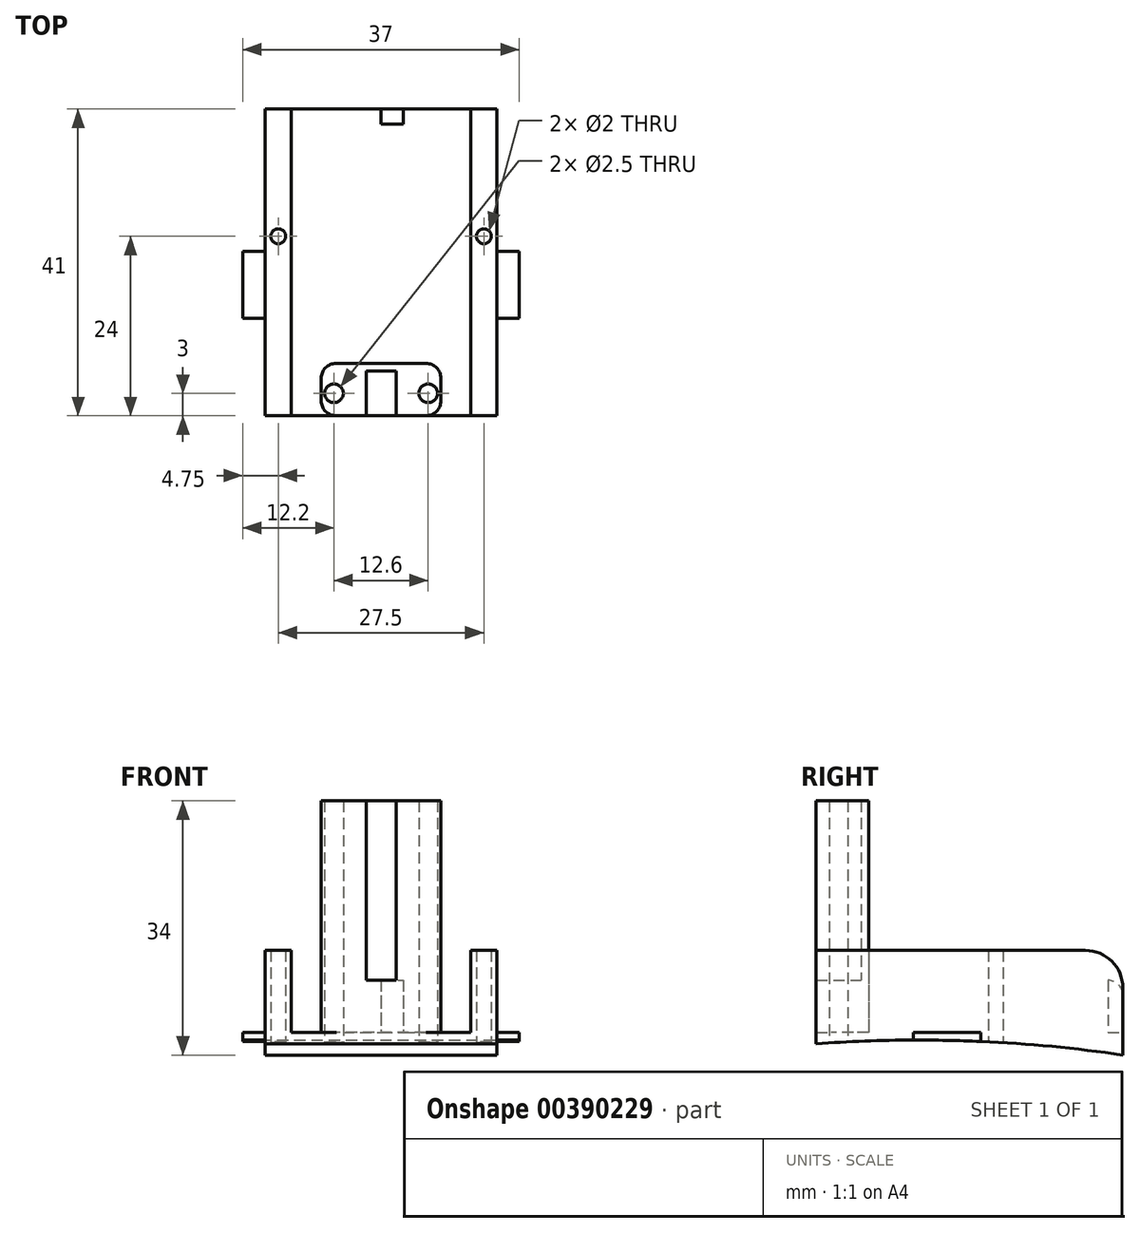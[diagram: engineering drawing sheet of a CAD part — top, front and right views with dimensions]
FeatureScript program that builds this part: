
annotation { "Feature Type Name" : "Feature", "Feature Type Description" : "" }
export const myFeature = defineFeature(function(context is Context, id is Id, definition is map)
    precondition{}
    {
        {
            var Q0;
            Q0=qCreatedBy(makeId("Top.planeOp"),FACE);
            var sketch = newSketch(context, id + "F0", { "sketchPlane" : qUnion([Q0])});
            skLineSegment(sketch, "E0", {"start": v(-15.5, 41) * mm, "end": v(15.5, 41) * mm});
            skLineSegment(sketch, "E1", {"start": v(15.5, 41) * mm, "end": v(15.5, 0) * mm});
            skLineSegment(sketch, "E2", {"start": v(15.5, 0) * mm, "end": v(-15.5, 0) * mm});
            skLineSegment(sketch, "E3", {"start": v(-15.5, 0) * mm, "end": v(-15.5, 41) * mm});
            skLineSegment(sketch, "E4", {"start": v(-12, 41) * mm, "end": v(-12, 0) * mm});
            skLineSegment(sketch, "E5", {"start": v(12, 41) * mm, "end": v(12, 0) * mm});
            skPoint(sketch, "E6.endSnap0", {"position": v(0, 41) * mm});
            skLineSegment(sketch, "E7", {"start": v(0, 39) * mm, "end": v(0, 41) * mm});
            skLineSegment(sketch, "E8", {"start": v(12, 7) * mm, "end": v(-12, 7) * mm});
            skLineSegment(sketch, "E9", {"start": v(-2, 0) * mm, "end": v(-2, 6) * mm});
            skLineSegment(sketch, "E10", {"start": v(-2, 6) * mm, "end": v(2, 6) * mm});
            skLineSegment(sketch, "E11", {"start": v(2, 6) * mm, "end": v(2, 0) * mm});
            skPoint(sketch, "E12", {"position": v(6.3, 3) * mm});
            skPoint(sketch, "E12.positionSnap0", {"position": v(2, 3) * mm});
            skPoint(sketch, "E13", {"position": v(-6.3, 3) * mm});
            skPoint(sketch, "E13.positionSnap0", {"position": v(-2, 3) * mm});
            skLineSegment(sketch, "E14", {"start": v(-15.5, 22) * mm, "end": v(-18.5, 22) * mm});
            skLineSegment(sketch, "E15", {"start": v(-18.5, 22) * mm, "end": v(-18.5, 13) * mm});
            skLineSegment(sketch, "E16", {"start": v(-18.5, 13) * mm, "end": v(-15.5, 13) * mm});
            skLineSegment(sketch, "E17", {"start": v(15.5, 22) * mm, "end": v(18.5, 22) * mm});
            skLineSegment(sketch, "E18", {"start": v(18.5, 22) * mm, "end": v(18.5, 13) * mm});
            skLineSegment(sketch, "E19", {"start": v(18.5, 13) * mm, "end": v(15.5, 13) * mm});
            skLineSegment(sketch, "E20", {"start": v(0, 39) * mm, "end": v(3, 39) * mm});
            skLineSegment(sketch, "E21", {"start": v(3, 39) * mm, "end": v(3, 41) * mm});
            skLineSegment(sketch, "E22", {"start": v(8, 7) * mm, "end": v(8, 0) * mm});
            skLineSegment(sketch, "E23", {"start": v(-8, 7) * mm, "end": v(-8, 0) * mm});
            skPoint(sketch, "E24", {"position": v(-13.75, 24) * mm});
            skPoint(sketch, "E25", {"position": v(13.75, 24) * mm});
            skSolve(sketch);
        }
        {
            var Q0;
            {var subQ3=sQuery(id+"F0.wireOp",EDGE,"E23");Q0=makeQuery(id+"F0.imprint","IMPRINT",FACE,{"disambiguationData":[TD([[makeQuery(id+"F0.imprint","IMPRINT",EDGE,{"derivedFrom":subQ3}),-1.0]])]});}
            var Q1;
            {var subQ10=sQuery(id+"F0.wireOp",EDGE,"E7");Q1=makeQuery(id+"F0.imprint","IMPRINT",FACE,{"disambiguationData":[TD([[makeQuery(id+"F0.imprint","IMPRINT",EDGE,{"derivedFrom":subQ10}),1.0]])]});}
            var Q2;
            {var subQ3=sQuery(id+"F0.wireOp",EDGE,"E22");Q2=makeQuery(id+"F0.imprint","IMPRINT",FACE,{"disambiguationData":[TD([[makeQuery(id+"F0.imprint","IMPRINT",EDGE,{"derivedFrom":subQ3}),1.0]])]});}
            extrude(context, id + "F1", {"entities" : qUnion([Q0, Q1, Q2]), "depth" : 3 * mm});
        }
        {
            var Q0;
            {var subQ0=sQuery(id+"F0.wireOp",EDGE,"E3");var subQ7=sQuery(id+"F0.wireOp",EDGE,"E0");var subQ8=makeQuery(id+"F0.imprint","INTERSECT",VERTEX,{"derivedFrom":[subQ7,subQ0]});Q0=makeQuery(id+"F0.imprint","IMPRINT",FACE,{"disambiguationData":[TD([[makeQuery(id+"F0.imprint","IMPRINT",EDGE,{"disambiguationData":[TD([[subQ8,-1.0]])],"derivedFrom":subQ7}),-1.0]])]});}
            var Q1;
            {var subQ1=sQuery(id+"F0.wireOp",EDGE,"E1");var subQ5=sQuery(id+"F0.wireOp",EDGE,"E0");var subQ6=makeQuery(id+"F0.imprint","INTERSECT",VERTEX,{"derivedFrom":[subQ5,subQ1]});Q1=makeQuery(id+"F0.imprint","IMPRINT",FACE,{"disambiguationData":[TD([[makeQuery(id+"F0.imprint","IMPRINT",EDGE,{"disambiguationData":[TD([[subQ6,1.0]])],"derivedFrom":subQ5}),-1.0]])]});}
            extrude(context, id + "F2", {"entities" : qUnion([Q0, Q1]), "operationType" : NewBodyOperationType.ADD, "depth" : 14 * mm});
        }
        {
            var Q0;
            {var subQ0=sQuery(id+"F0.wireOp",EDGE,"E14");Q0=makeQuery(id+"F0.imprint","IMPRINT",FACE,{"disambiguationData":[TD([[makeQuery(id+"F0.imprint","IMPRINT",EDGE,{"derivedFrom":subQ0}),1.0]])]});}
            var Q1;
            {var subQ0=sQuery(id+"F0.wireOp",EDGE,"E17");Q1=makeQuery(id+"F0.imprint","IMPRINT",FACE,{"disambiguationData":[TD([[makeQuery(id+"F0.imprint","IMPRINT",EDGE,{"derivedFrom":subQ0}),-1.0]])]});}
            extrude(context, id + "F3", {"entities" : qUnion([Q0, Q1]), "operationType" : NewBodyOperationType.ADD, "depth" : 3 * mm});
        }
        {
            var Q0;
            {var subQ0=sQuery(id+"F0.wireOp",EDGE,"E9");Q0=makeQuery(id+"F0.imprint","IMPRINT",FACE,{"disambiguationData":[TD([[makeQuery(id+"F0.imprint","IMPRINT",EDGE,{"derivedFrom":subQ0}),1.0]])]});}
            extrude(context, id + "F4", {"entities" : qUnion([Q0]), "operationType" : NewBodyOperationType.ADD, "depth" : 34 * mm});
        }
        {
            var Q0;
            {var subQ0=sQuery(id+"F0.wireOp",EDGE,"E9");Q0=makeQuery(id+"F0.imprint","IMPRINT",FACE,{"disambiguationData":[TD([[makeQuery(id+"F0.imprint","IMPRINT",EDGE,{"derivedFrom":subQ0}),-1.0]])]});}
            extrude(context, id + "F5", {"entities" : qUnion([Q0]), "operationType" : NewBodyOperationType.ADD, "depth" : 10 * mm});
        }
        {
            var Q0;
            Q0=makeQuery(id+"F5.opExtrude","CAP_EDGE",EDGE,{"disambiguationData":[OSD([sQuery(id+"F0.wireOp",EDGE,"E10")])],"isStart":false});
            var Q1;
            {var subQ0=sQuery(id+"F0.wireOp",EDGE,"E0");Q1=makeQuery(id+"F2.opExtrude","CAP_EDGE",EDGE,{"disambiguationData":[OSD([subQ0]),TDD([makeQuery(id+"F0.imprint","IMPRINT",EDGE,{"disambiguationData":[TD([[makeQuery(id+"F0.imprint","INTERSECT",VERTEX,{"derivedFrom":[subQ0,sQuery(id+"F0.wireOp",EDGE,"E3")]}),-1.0]])],"derivedFrom":subQ0})])],"isStart":false});}
            var Q2;
            {var subQ0=sQuery(id+"F0.wireOp",EDGE,"E0");Q2=makeQuery(id+"F2.opExtrude","CAP_EDGE",EDGE,{"disambiguationData":[OSD([subQ0]),TDD([makeQuery(id+"F0.imprint","IMPRINT",EDGE,{"disambiguationData":[TD([[makeQuery(id+"F0.imprint","INTERSECT",VERTEX,{"derivedFrom":[subQ0,sQuery(id+"F0.wireOp",EDGE,"E1")]}),1.0]])],"derivedFrom":subQ0})])],"isStart":false});}
            fillet(context, id + "F6", {"entities" : qUnion([Q0, Q1, Q2]), "radius" : 5 * mm, "tangentPropagation" : true, "allowEdgeOverflow" : false});
        }
        {
            var Q0;
            {var subQ0=sQuery(id+"F0.wireOp",EDGE,"E7");Q0=makeQuery(id+"F0.imprint","IMPRINT",FACE,{"disambiguationData":[TD([[makeQuery(id+"F0.imprint","IMPRINT",EDGE,{"derivedFrom":subQ0}),-1.0]])]});}
            extrude(context, id + "F7", {"entities" : qUnion([Q0]), "operationType" : NewBodyOperationType.ADD, "depth" : 10 * mm});
        }
        {
            var Q0;
            Q0=makeQuery(id+"F1.opExtrude","CAP_EDGE",EDGE,{"disambiguationData":[OSD([sQuery(id+"F0.wireOp",EDGE,"E23")])],"isStart":false});
            var Q1;
            Q1=makeQuery(id+"F1.opExtrude","CAP_EDGE",EDGE,{"disambiguationData":[OSD([sQuery(id+"F0.wireOp",EDGE,"E22")])],"isStart":false});
            var Q2;
            Q2=makeQuery(id+"F1.opExtrude","CAP_EDGE",EDGE,{"disambiguationData":[OSD([sQuery(id+"F0.wireOp",EDGE,"E4")])],"isStart":false});
            var Q3;
            Q3=makeQuery(id+"F1.opExtrude","CAP_EDGE",EDGE,{"disambiguationData":[OSD([sQuery(id+"F0.wireOp",EDGE,"E5")])],"isStart":false});
            var Q4;
            Q4=makeQuery(id+"F1.opExtrude","CAP_EDGE",EDGE,{"disambiguationData":[OSD([sQuery(id+"F0.wireOp",EDGE,"E8")])],"isStart":false});
            var Q5;
            Q5=makeQuery(id+"F1.opExtrude","CAP_EDGE",EDGE,{"disambiguationData":[OSD([sQuery(id+"F0.wireOp",EDGE,"E20")])],"isStart":false});
            var Q6;
            Q6=makeQuery(id+"F7.opExtrude","CAP_EDGE",EDGE,{"disambiguationData":[OSD([sQuery(id+"F0.wireOp",EDGE,"E0")])],"isStart":false});
            var Q7;
            Q7=makeQuery(id+"F4.opExtrude","SWEPT_EDGE",EDGE,{"disambiguationData":[OSD([sQuery(id+"F0.wireOp",EDGE,"E8"),sQuery(id+"F0.wireOp",EDGE,"E22")])]});
            var Q8;
            Q8=makeQuery(id+"F4.opExtrude","SWEPT_EDGE",EDGE,{"disambiguationData":[OSD([sQuery(id+"F0.wireOp",EDGE,"E8"),sQuery(id+"F0.wireOp",EDGE,"E23")])]});
            var Q9;
            Q9=makeQuery(id+"F4.opExtrude","SWEPT_EDGE",EDGE,{"disambiguationData":[OSD([sQuery(id+"F0.wireOp",EDGE,"E2"),sQuery(id+"F0.wireOp",EDGE,"E22")])]});
            var Q10;
            Q10=makeQuery(id+"F4.opExtrude","SWEPT_EDGE",EDGE,{"disambiguationData":[OSD([sQuery(id+"F0.wireOp",EDGE,"E2"),sQuery(id+"F0.wireOp",EDGE,"E23")])]});
            fillet(context, id + "F8", {"entities" : qUnion([Q0, Q1, Q2, Q3, Q4, Q5, Q6, Q7, Q8, Q9, Q10]), "radius" : 2 * mm, "tangentPropagation" : true, "allowEdgeOverflow" : false});
        }
        {
            var Q0;
            Q0=qCreatedBy(makeId("Right.planeOp"),FACE);
            cPlane(context, id + "F9", {"entities" : qUnion([Q0]), "cplaneType" : CPlaneType.OFFSET, "offset" : 18.9 * mm, "width" : 150 * mm, "height" : 150 * mm});
        }
        {
            var Q0;
            Q0=qCreatedBy(id+"F9.planeOp",FACE);
            var sketch = newSketch(context, id + "F10", { "sketchPlane" : qUnion([Q0])});
            skLineSegment(sketch, "E26", {"start": v(41, 0) * mm, "end": v(0, 0) * mm});
            skLineSegment(sketch, "E27", {"start": v(0, 0) * mm, "end": v(0, 1.5) * mm});
            skArc(sketch, "E28", {"start": v(41, 0) * mm, "mid": v(20.54, 1.87) * mm, "end": v(0, 1.5) * mm});
            skSolve(sketch);
        }
        {
            var Q0;
            Q0=makeQuery(id+"F10.imprint","IMPRINT",FACE,{"disambiguationData":[TD([[makeQuery(id+"F10.imprint","IMPRINT",EDGE,{"derivedFrom":sQuery(id+"F10.wireOp",EDGE,"q8iaQYBd-D0QU-K8Ez-FoIt-P6ilia72zXyT")}),1.0]])]});
            var Q1;
            Q1=makeQuery(id+"F10.imprint","IMPRINT",FACE,{"disambiguationData":[TD([[makeQuery(id+"F10.imprint","IMPRINT",EDGE,{"derivedFrom":sQuery(id+"F10.wireOp",EDGE,"E26")}),-1.0]])]});
            extrude(context, id + "F11", {"entities" : qUnion([Q0, Q1]), "operationType" : NewBodyOperationType.REMOVE, "endBound" : BoundingType.THROUGH_ALL, "oppositeDirection" : true, "depth" : 25 * mm});
        }
        {
            var Q0;
            Q0=sQuery(id+"F0.wireOp",VERTEX,"E24");
            var Q1;
            Q1=sQuery(id+"F0.wireOp",VERTEX,"E25");
            var Q2;
            Q2=makeQuery(id+"F1.opExtrude","SWEPT_BODY",BODY,{"disambiguationData":[OSD([sQuery(id+"F0.wireOp",EDGE,"E0"),sQuery(id+"F0.wireOp",EDGE,"E2"),sQuery(id+"F0.wireOp",EDGE,"E4"),sQuery(id+"F0.wireOp",EDGE,"E5"),sQuery(id+"F0.wireOp",EDGE,"E7"),sQuery(id+"F0.wireOp",EDGE,"E8"),sQuery(id+"F0.wireOp",EDGE,"E20"),sQuery(id+"F0.wireOp",EDGE,"E21"),sQuery(id+"F0.wireOp",EDGE,"E22"),sQuery(id+"F0.wireOp",EDGE,"E23")])]});
            hole(context, id + "F12", {"style" : HoleStyle.SIMPLE, "endStyle" : HoleEndStyle.THROUGH, "oppositeDirection" : true, "holeDiameter" : 2 * mm, "isTappedThrough" : true, "tappedDepth" : 12 * mm, "tapClearance" : 3, "locations" : qUnion([Q0, Q1]), "scope" : qUnion([Q2])});
        }
        {
            var Q0;
            Q0=sQuery(id+"F0.wireOp",VERTEX,"E13");
            var Q1;
            Q1=sQuery(id+"F0.wireOp",VERTEX,"E12");
            var Q2;
            Q2=makeQuery(id+"F1.opExtrude","SWEPT_BODY",BODY,{"disambiguationData":[OSD([sQuery(id+"F0.wireOp",EDGE,"E0"),sQuery(id+"F0.wireOp",EDGE,"E2"),sQuery(id+"F0.wireOp",EDGE,"E4"),sQuery(id+"F0.wireOp",EDGE,"E5"),sQuery(id+"F0.wireOp",EDGE,"E7"),sQuery(id+"F0.wireOp",EDGE,"E8"),sQuery(id+"F0.wireOp",EDGE,"E20"),sQuery(id+"F0.wireOp",EDGE,"E21"),sQuery(id+"F0.wireOp",EDGE,"E22"),sQuery(id+"F0.wireOp",EDGE,"E23")])]});
            hole(context, id + "F13", {"style" : HoleStyle.SIMPLE, "endStyle" : HoleEndStyle.THROUGH, "oppositeDirection" : true, "holeDiameter" : 2.5 * mm, "isTappedThrough" : true, "tappedDepth" : 12 * mm, "tapClearance" : 3, "locations" : qUnion([Q0, Q1]), "scope" : qUnion([Q2])});
        }
    });
